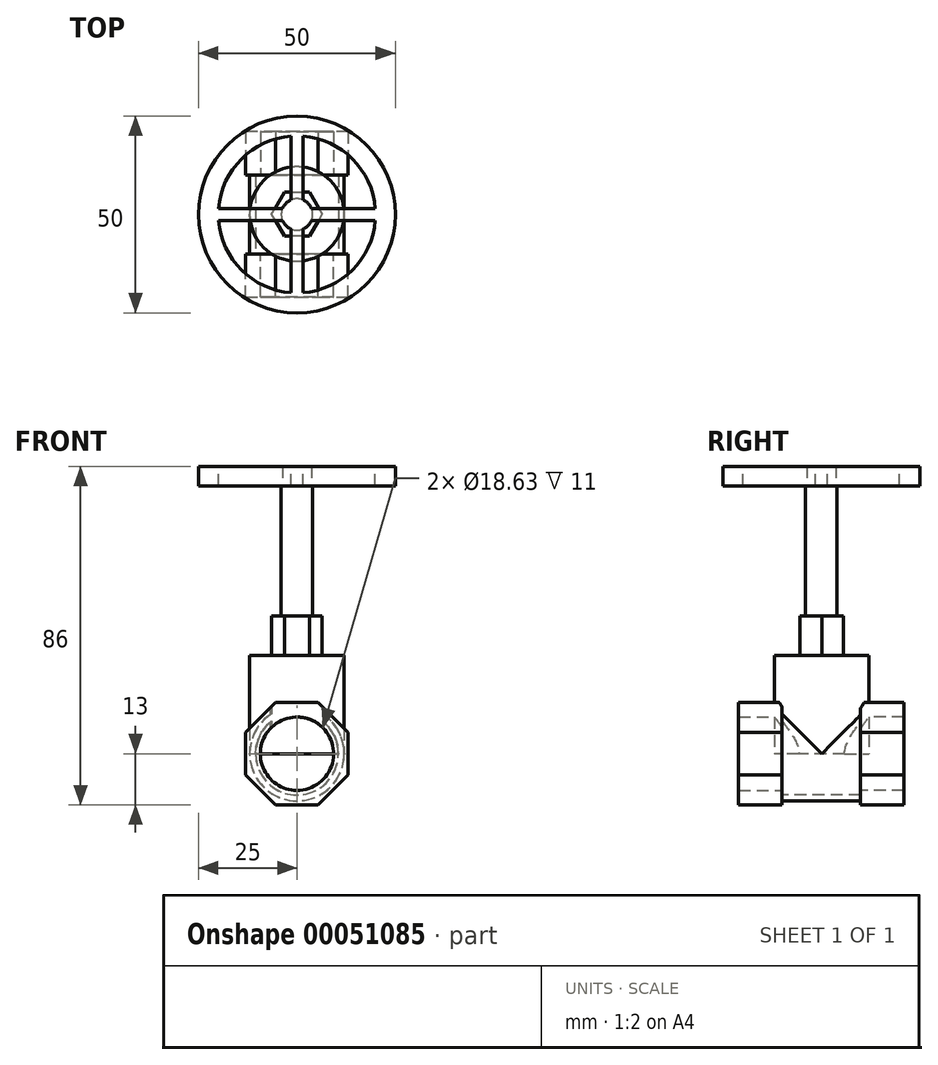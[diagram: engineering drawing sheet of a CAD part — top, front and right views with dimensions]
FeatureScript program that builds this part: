
annotation { "Feature Type Name" : "Feature", "Feature Type Description" : "" }
export const myFeature = defineFeature(function(context is Context, id is Id, definition is map)
    precondition{}
    {
        {
            var Q0;
            Q0=qCreatedBy(makeId("Front.planeOp"),FACE);
            var sketch = newSketch(context, id + "F0", { "sketchPlane" : qUnion([Q0])});
            skCircle(sketch, "E0", {"center": v(0, 0) * mm, "radius": 9.32 * mm});
            skCircle(sketch, "E1.cCircle", {"center": v(0, 0) * mm, "radius": 13 * mm, "construction": true});
            skLineSegment(sketch, "E1.0", {"start": v(13, 5.38) * mm, "end": v(13, -5.38) * mm});
            skLineSegment(sketch, "E1.1", {"start": v(13, -5.38) * mm, "end": v(5.38, -13) * mm});
            skLineSegment(sketch, "E1.2", {"start": v(5.38, -13) * mm, "end": v(-5.38, -13) * mm});
            skLineSegment(sketch, "E1.3", {"start": v(-5.38, -13) * mm, "end": v(-13, -5.38) * mm});
            skLineSegment(sketch, "E1.4", {"start": v(-13, -5.38) * mm, "end": v(-13, 5.38) * mm});
            skLineSegment(sketch, "E1.5", {"start": v(-13, 5.38) * mm, "end": v(-5.38, 13) * mm});
            skLineSegment(sketch, "E1.6", {"start": v(-5.38, 13) * mm, "end": v(5.38, 13) * mm});
            skLineSegment(sketch, "E1.7", {"start": v(5.38, 13) * mm, "end": v(13, 5.38) * mm});
            skPoint(sketch, "E1.0.midPoint", {"position": v(13, 0) * mm});
            skSolve(sketch);
        }
        {
            var Q0;
            Q0=qSketchRegion(id+"F0",true);
            extrude(context, id + "F1", {"entities" : qUnion([Q0]), "depth" : 11 * mm});
        }
        {
            var Q0;
            Q0=makeQuery(id+"F1.opExtrude","CAP_FACE",FACE,{"disambiguationData":[OSD([sQuery(id+"F0.wireOp",EDGE,"E0"),sQuery(id+"F0.wireOp",EDGE,"E1.0"),sQuery(id+"F0.wireOp",EDGE,"E1.1"),sQuery(id+"F0.wireOp",EDGE,"E1.2"),sQuery(id+"F0.wireOp",EDGE,"E1.3"),sQuery(id+"F0.wireOp",EDGE,"E1.4"),sQuery(id+"F0.wireOp",EDGE,"E1.5"),sQuery(id+"F0.wireOp",EDGE,"E1.6"),sQuery(id+"F0.wireOp",EDGE,"E1.7")])],"isStart":true});
            var sketch = newSketch(context, id + "F2", { "sketchPlane" : qUnion([Q0])});
            skCircle(sketch, "E2", {"center": v(0, 0) * mm, "radius": 12 * mm});
            skCircle(sketch, "E3", {"center": v(0, 0) * mm, "radius": 10.5 * mm});
            skSolve(sketch);
        }
        {
            var Q0;
            Q0=qSketchRegion(id+"F2",true);
            extrude(context, id + "F3", {"entities" : qUnion([Q0]), "operationType" : NewBodyOperationType.ADD, "depth" : (42 - 22) * mm});
        }
        {
            var Q0;
            Q0=makeQuery(id+"F3.opExtrude","CAP_FACE",FACE,{"disambiguationData":[OSD([sQuery(id+"F2.wireOp",EDGE,"E2"),sQuery(id+"F2.wireOp",EDGE,"E3")])],"isStart":false});
            var sketch = newSketch(context, id + "F4", { "sketchPlane" : qUnion([Q0])});
            skCircle(sketch, "E4", {"center": v(0, 0) * mm, "radius": 9.32 * mm});
            skCircle(sketch, "E5.cCircle", {"center": v(0, 0) * mm, "radius": 13 * mm, "construction": true});
            skLineSegment(sketch, "E5.0", {"start": v(13, 5.38) * mm, "end": v(13, -5.38) * mm});
            skLineSegment(sketch, "E5.1", {"start": v(13, -5.38) * mm, "end": v(5.38, -13) * mm});
            skLineSegment(sketch, "E5.2", {"start": v(5.38, -13) * mm, "end": v(-5.38, -13) * mm});
            skLineSegment(sketch, "E5.3", {"start": v(-5.38, -13) * mm, "end": v(-13, -5.38) * mm});
            skLineSegment(sketch, "E5.4", {"start": v(-13, -5.38) * mm, "end": v(-13, 5.38) * mm});
            skLineSegment(sketch, "E5.5", {"start": v(-13, 5.38) * mm, "end": v(-5.38, 13) * mm});
            skLineSegment(sketch, "E5.6", {"start": v(-5.38, 13) * mm, "end": v(5.38, 13) * mm});
            skLineSegment(sketch, "E5.7", {"start": v(5.38, 13) * mm, "end": v(13, 5.38) * mm});
            skPoint(sketch, "E5.0.midPoint", {"position": v(13, 0) * mm});
            skSolve(sketch);
        }
        {
            var Q0;
            Q0=qSketchRegion(id+"F4",true);
            extrude(context, id + "F5", {"entities" : qUnion([Q0]), "operationType" : NewBodyOperationType.ADD, "depth" : 11 * mm});
        }
        {
            var Q0;
            Q0=qCreatedBy(makeId("Top.planeOp"),FACE);
            var sketch = newSketch(context, id + "F6", { "sketchPlane" : qUnion([Q0])});
            skCircle(sketch, "E6", {"center": v(0, 10.11) * mm, "radius": 12 * mm});
            skSolve(sketch);
        }
        {
            var Q0;
            Q0=qSketchRegion(id+"F6",true);
            extrude(context, id + "F7", {"entities" : qUnion([Q0]), "operationType" : NewBodyOperationType.ADD, "depth" : 25 * mm});
        }
        {
            var Q0;
            Q0=makeQuery(id+"F7.opExtrude","CAP_FACE",FACE,{"disambiguationData":[OSD([sQuery(id+"F6.wireOp",EDGE,"E6")])],"isStart":false});
            var sketch = newSketch(context, id + "F8", { "sketchPlane" : qUnion([Q0])});
            skCircle(sketch, "E7.cCircle", {"center": v(0, 10.11) * mm, "radius": 5.55 * mm, "construction": true});
            skLineSegment(sketch, "E7.0", {"start": v(3.2, 4.57) * mm, "end": v(-3.2, 4.57) * mm});
            skLineSegment(sketch, "E7.1", {"start": v(-3.2, 4.57) * mm, "end": v(-6.4, 10.11) * mm});
            skLineSegment(sketch, "E7.2", {"start": v(-6.4, 10.11) * mm, "end": v(-3.2, 15.66) * mm});
            skLineSegment(sketch, "E7.3", {"start": v(-3.2, 15.66) * mm, "end": v(3.2, 15.66) * mm});
            skLineSegment(sketch, "E7.4", {"start": v(3.2, 15.66) * mm, "end": v(6.4, 10.11) * mm});
            skLineSegment(sketch, "E7.5", {"start": v(6.4, 10.11) * mm, "end": v(3.2, 4.57) * mm});
            skPoint(sketch, "E7.0.midPoint", {"position": v(0, 4.57) * mm});
            skSolve(sketch);
        }
        {
            var Q0;
            Q0=qSketchRegion(id+"F8",true);
            extrude(context, id + "F9", {"entities" : qUnion([Q0]), "operationType" : NewBodyOperationType.ADD, "depth" : 10 * mm});
        }
        {
            var Q0;
            Q0=qCreatedBy(makeId("Top.planeOp"),FACE);
            var sketch = newSketch(context, id + "F10", { "sketchPlane" : qUnion([Q0])});
            skCircle(sketch, "E8", {"center": v(0, 10) * mm, "radius": 4 * mm});
            skSolve(sketch);
        }
        {
            var Q0;
            Q0=qSketchRegion(id+"F10",true);
            extrude(context, id + "F11", {"entities" : qUnion([Q0]), "operationType" : NewBodyOperationType.ADD, "depth" : 73 * mm});
        }
        {
            var Q0;
            Q0=makeQuery(id+"F11.opExtrude","CAP_FACE",FACE,{"disambiguationData":[OSD([sQuery(id+"F10.wireOp",EDGE,"E8")])],"isStart":false});
            var sketch = newSketch(context, id + "F12", { "sketchPlane" : qUnion([Q0])});
            skLineSegment(sketch, "E9.bottom", {"start": v(-1.87, 11.5) * mm, "end": v(-19.94, 11.5) * mm});
            skLineSegment(sketch, "E9.top", {"start": v(-1.87, 8.5) * mm, "end": v(-19.94, 8.5) * mm});
            skLineSegment(sketch, "E9.left", {"start": v(-1.87, 11.5) * mm, "end": v(-1.87, 8.5) * mm});
            skLineSegment(sketch, "E9.right", {"start": v(-19.94, 11.5) * mm, "end": v(-19.94, 8.5) * mm});
            skLineSegment(sketch, "E10.bottom", {"start": v(1.55, 11.5) * mm, "end": v(19.94, 11.5) * mm});
            skLineSegment(sketch, "E10.top", {"start": v(1.55, 8.5) * mm, "end": v(19.94, 8.5) * mm});
            skLineSegment(sketch, "E10.left", {"start": v(1.55, 11.5) * mm, "end": v(1.55, 8.5) * mm});
            skLineSegment(sketch, "E10.right", {"start": v(19.94, 11.5) * mm, "end": v(19.94, 8.5) * mm});
            skLineSegment(sketch, "E11.bottom", {"start": v(1.5, 7.45) * mm, "end": v(-1.5, 7.45) * mm});
            skLineSegment(sketch, "E11.top", {"start": v(1.5, -9.94) * mm, "end": v(-1.5, -9.94) * mm});
            skLineSegment(sketch, "E11.left", {"start": v(1.5, 7.45) * mm, "end": v(1.5, -9.94) * mm});
            skLineSegment(sketch, "E11.right", {"start": v(-1.5, 7.45) * mm, "end": v(-1.5, -9.94) * mm});
            skLineSegment(sketch, "E12.bottom", {"start": v(-1.5, 12.78) * mm, "end": v(1.5, 12.78) * mm});
            skLineSegment(sketch, "E12.top", {"start": v(-1.5, 29.94) * mm, "end": v(1.5, 29.94) * mm});
            skLineSegment(sketch, "E12.left", {"start": v(-1.5, 12.78) * mm, "end": v(-1.5, 29.94) * mm});
            skLineSegment(sketch, "E12.right", {"start": v(1.5, 12.78) * mm, "end": v(1.5, 29.94) * mm});
            skSolve(sketch);
        }
        {
            var Q0;
            Q0=qSketchRegion(id+"F12",true);
            extrude(context, id + "F13", {"entities" : qUnion([Q0]), "operationType" : NewBodyOperationType.ADD, "oppositeDirection" : true, "depth" : 5 * mm});
        }
        {
            var Q0;
            Q0=makeQuery(id+"F13.boolean.opBoolean","MERGE",FACE,{"derivedFrom":[makeQuery(id+"F11.opExtrude","CAP_FACE",FACE,{"disambiguationData":[OSD([sQuery(id+"F10.wireOp",EDGE,"E8")])],"isStart":false}),makeQuery(id+"F13.opExtrude","CAP_FACE",FACE,{"disambiguationData":[OSD([sQuery(id+"F12.wireOp",EDGE,"E9.bottom"),sQuery(id+"F12.wireOp",EDGE,"E9.top"),sQuery(id+"F12.wireOp",EDGE,"E9.left"),sQuery(id+"F12.wireOp",EDGE,"E9.right")])],"isStart":true}),makeQuery(id+"F13.opExtrude","CAP_FACE",FACE,{"disambiguationData":[OSD([sQuery(id+"F12.wireOp",EDGE,"E10.bottom"),sQuery(id+"F12.wireOp",EDGE,"E10.top"),sQuery(id+"F12.wireOp",EDGE,"E10.left"),sQuery(id+"F12.wireOp",EDGE,"E10.right")])],"isStart":true}),makeQuery(id+"F13.opExtrude","CAP_FACE",FACE,{"disambiguationData":[OSD([sQuery(id+"F12.wireOp",EDGE,"E11.bottom"),sQuery(id+"F12.wireOp",EDGE,"E11.top"),sQuery(id+"F12.wireOp",EDGE,"E11.left"),sQuery(id+"F12.wireOp",EDGE,"E11.right")])],"isStart":true}),makeQuery(id+"F13.opExtrude","CAP_FACE",FACE,{"disambiguationData":[OSD([sQuery(id+"F12.wireOp",EDGE,"E12.bottom"),sQuery(id+"F12.wireOp",EDGE,"E12.top"),sQuery(id+"F12.wireOp",EDGE,"E12.left"),sQuery(id+"F12.wireOp",EDGE,"E12.right")])],"isStart":true})]});
            var sketch = newSketch(context, id + "F14", { "sketchPlane" : qUnion([Q0])});
            skCircle(sketch, "E13", {"center": v(0, 10) * mm, "radius": 19.94 * mm});
            skCircle(sketch, "E14", {"center": v(0, 10) * mm, "radius": 25 * mm});
            skSolve(sketch);
        }
        {
            var Q0;
            Q0=qSketchRegion(id+"F14",true);
            extrude(context, id + "F15", {"entities" : qUnion([Q0]), "operationType" : NewBodyOperationType.ADD, "oppositeDirection" : true, "depth" : 5 * mm});
        }
    });
